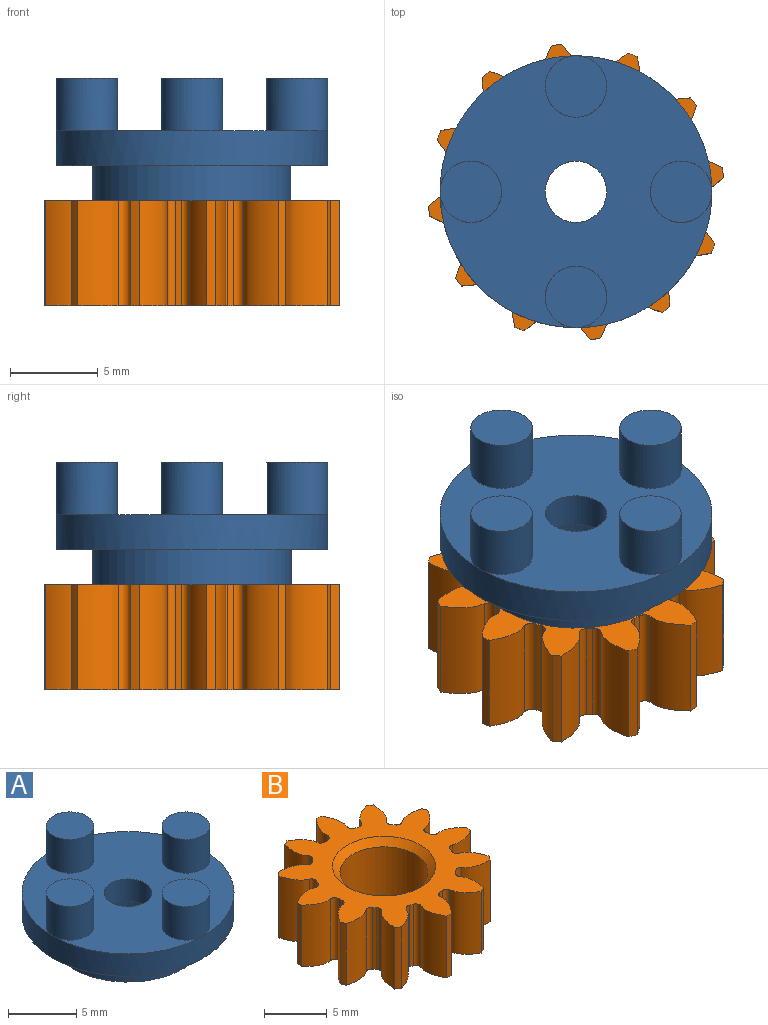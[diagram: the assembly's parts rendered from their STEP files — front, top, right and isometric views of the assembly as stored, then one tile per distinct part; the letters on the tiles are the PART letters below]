
ASSEMBLY  parts=2 mates=1
PART A: 16 faces, bbox 22.5x22.5x14 mm
  f0: plane 7x7mm, normal (0,0,-1), area 28.9mm2, adj f1,f13
  f1: cylinder r=1.75mm len=3.5mm, axis (0,0,-1), area 22mm2, adj f0,f3
  f2: cylinder r=7.75mm len=15.5mm, axis (0,0,-1), area 97.4mm2, adj f3,f4
  f3: plane 15.5x15.5mm, normal (0,0,1), area 140.6mm2, adj f1,f2,f5,f7,f9,f11
  f4: plane 15.5x15.5mm, normal (0,0,-1), area 88.4mm2, adj f2,f14
  f5: cylinder r=1.75mm len=3.5mm, axis (0,0,-1), area 33mm2, adj f3,f6
  f6: plane 3.5x3.5mm, normal (0,0,1), area 9.6mm2, adj f5
  f7: cylinder r=1.75mm len=3.5mm, axis (0,0,-1), area 33mm2, adj f3,f8
  f8: plane 10.5x10.5mm, normal (0,0,1), area 19.2mm2, adj f7
  f9: cylinder r=1.75mm len=3.5mm, axis (0,0,-1), area 33mm2, adj f3,f10
  f10: plane 3.5x3.5mm, normal (0,0,1), area 9.6mm2, adj f9
  f11: cylinder r=1.75mm len=3.5mm, axis (0,0,-1), area 33mm2, adj f3,f12
  f12: plane 3.5x3.5mm, normal (0,0,1), area 9.6mm2, adj f11
  f13: cylinder r=3.5mm len=7mm, axis (0,0,1), area 44mm2, adj f0,f15
  f14: cylinder r=5.65mm len=11.3mm, axis (0,0,1), area 71mm2, adj f4,f15
  f15: plane 11.3x11.3mm, normal (0,0,-1), area 61.8mm2, adj f13,f14
PART B: 76 faces, bbox 16.9x16.9x6 mm
  f0: cylinder r=8.46mm len=6mm, axis (0,0,-1), area 3.2mm2, adj f11,f14,f62,f71
  f1: cylinder r=8.46mm len=6mm, axis (0,0,-1), area 3.2mm2, adj f11,f14,f66,f72
  f2: cylinder r=8.46mm len=6mm, axis (0,0,-1), area 3.2mm2, adj f11,f14,f57,f61
  f3: cylinder r=8.46mm len=6mm, axis (0,0,-1), area 3.2mm2, adj f11,f14,f52,f56
  f4: cylinder r=8.46mm len=6mm, axis (0,0,-1), area 3.2mm2, adj f11,f14,f47,f51
  f5: cylinder r=8.46mm len=6mm, axis (0,0,-1), area 3.2mm2, adj f11,f14,f37,f46
  f6: cylinder r=8.46mm len=6mm, axis (0,0,-1), area 3.2mm2, adj f11,f14,f17,f41
  f7: cylinder r=8.46mm len=6mm, axis (0,0,-1), area 3.2mm2, adj f11,f14,f36,f42
  f8: cylinder r=8.46mm len=6mm, axis (0,0,-1), area 3.2mm2, adj f11,f14,f27,f31
  f9: cylinder r=8.46mm len=6mm, axis (0,0,-1), area 3.2mm2, adj f11,f14,f22,f26
  f10: cylinder r=8.46mm len=6mm, axis (0,0,-1), area 3.2mm2, adj f11,f14,f21,f67
  f11: plane 16.87x16.87mm, normal (0,0,1), area 106.9mm2, adj f0,f1,f2,f3,f4,f5,f6,f7
  f12: cylinder r=3.5mm len=7mm, axis (0,0,-1), area 118.8mm2, adj f14,f75
  f13: cylinder r=8.46mm len=6mm, axis (0,0,-1), area 3.2mm2, adj f11,f14,f16,f32
  f14: plane 16.87x16.87mm, normal (0,0,-1), area 121.2mm2, adj f0,f1,f2,f3,f4,f5,f6,f7
  f15: cylinder r=5.74mm len=6mm, axis (0,0,-1), area 2.2mm2, adj f11,f14,f18,f19
  f16: extruded ~6x2.27mm, area 15.5mm2, adj f11,f13,f14,f18
  f17: extruded ~6x1.92mm, area 15.5mm2, adj f6,f11,f14,f19
  f18: cylinder r=0.43mm len=6mm, axis (0,0,-1), area 3.9mm2, adj f11,f14,f15,f16
  f19: cylinder r=0.43mm len=6mm, axis (0,0,-1), area 3.9mm2, adj f11,f14,f15,f17
  f20: cylinder r=5.74mm len=6mm, axis (0,0,-1), area 2.2mm2, adj f11,f14,f23,f24
  f21: extruded ~6x2.27mm, area 15.5mm2, adj f10,f11,f14,f23
  f22: extruded ~6x1.92mm, area 15.5mm2, adj f9,f11,f14,f24
  f23: cylinder r=0.43mm len=6mm, axis (0,0,-1), area 3.9mm2, adj f11,f14,f20,f21
  f24: cylinder r=0.43mm len=6mm, axis (0,0,-1), area 3.9mm2, adj f11,f14,f20,f22
  f25: cylinder r=5.74mm len=6mm, axis (0,0,-1), area 2.2mm2, adj f11,f14,f28,f29
  f26: extruded ~6x2.47mm, area 15.5mm2, adj f9,f11,f14,f28
  f27: extruded ~6x2.33mm, area 15.5mm2, adj f8,f11,f14,f29
  f28: cylinder r=0.43mm len=6mm, axis (0,0,-1), area 3.9mm2, adj f11,f14,f25,f26
  f29: cylinder r=0.43mm len=6mm, axis (0,0,-1), area 3.9mm2, adj f11,f14,f25,f27
  f30: cylinder r=5.74mm len=6mm, axis (0,0,-1), area 2.2mm2, adj f11,f14,f33,f34
  f31: extruded ~6x2.02mm, area 15.5mm2, adj f8,f11,f14,f33
  f32: extruded ~6x2.45mm, area 15.5mm2, adj f11,f13,f14,f34
  f33: cylinder r=0.43mm len=6mm, axis (0,0,-1), area 3.9mm2, adj f11,f14,f30,f31
  f34: cylinder r=0.43mm len=6mm, axis (0,0,-1), area 3.9mm2, adj f11,f14,f30,f32
  f35: cylinder r=5.74mm len=6mm, axis (0,0,-1), area 2.2mm2, adj f11,f14,f38,f39
  f36: extruded ~6x2.02mm, area 15.5mm2, adj f7,f11,f14,f38
  f37: extruded ~6x2.45mm, area 15.5mm2, adj f5,f11,f14,f39
  f38: cylinder r=0.43mm len=6mm, axis (0,0,-1), area 3.9mm2, adj f11,f14,f35,f36
  f39: cylinder r=0.43mm len=6mm, axis (0,0,-1), area 3.9mm2, adj f11,f14,f35,f37
  f40: cylinder r=5.74mm len=6mm, axis (0,0,-1), area 2.2mm2, adj f11,f14,f43,f44
  f41: extruded ~6x2.47mm, area 15.5mm2, adj f6,f11,f14,f43
  f42: extruded ~6x2.33mm, area 15.5mm2, adj f7,f11,f14,f44
  f43: cylinder r=0.43mm len=6mm, axis (0,0,-1), area 3.9mm2, adj f11,f14,f40,f41
  f44: cylinder r=0.43mm len=6mm, axis (0,0,-1), area 3.9mm2, adj f11,f14,f40,f42
  f45: cylinder r=5.74mm len=6mm, axis (0,0,-1), area 2.2mm2, adj f11,f14,f48,f49
  f46: extruded ~6x2.27mm, area 15.5mm2, adj f5,f11,f14,f48
  f47: extruded ~6x1.92mm, area 15.5mm2, adj f4,f11,f14,f49
  f48: cylinder r=0.43mm len=6mm, axis (0,0,-1), area 3.9mm2, adj f11,f14,f45,f46
  f49: cylinder r=0.43mm len=6mm, axis (0,0,-1), area 3.9mm2, adj f11,f14,f45,f47
  f50: cylinder r=5.74mm len=6mm, axis (0,0,-1), area 2.2mm2, adj f11,f14,f53,f54
  f51: extruded ~6x2.47mm, area 15.5mm2, adj f4,f11,f14,f53
  f52: extruded ~6x2.33mm, area 15.5mm2, adj f3,f11,f14,f54
  f53: cylinder r=0.43mm len=6mm, axis (0,0,-1), area 3.9mm2, adj f11,f14,f50,f51
  f54: cylinder r=0.43mm len=6mm, axis (0,0,-1), area 3.9mm2, adj f11,f14,f50,f52
  f55: cylinder r=5.74mm len=6mm, axis (0,0,-1), area 2.2mm2, adj f11,f14,f58,f59
  f56: extruded ~6x2.02mm, area 15.5mm2, adj f3,f11,f14,f58
  f57: extruded ~6x2.45mm, area 15.5mm2, adj f2,f11,f14,f59
  f58: cylinder r=0.43mm len=6mm, axis (0,0,-1), area 3.9mm2, adj f11,f14,f55,f56
  f59: cylinder r=0.43mm len=6mm, axis (0,0,-1), area 3.9mm2, adj f11,f14,f55,f57
  f60: cylinder r=5.74mm len=6mm, axis (0,0,-1), area 2.2mm2, adj f11,f14,f63,f64
  f61: extruded ~6x2.27mm, area 15.5mm2, adj f2,f11,f14,f63
  f62: extruded ~6x1.92mm, area 15.5mm2, adj f0,f11,f14,f64
  f63: cylinder r=0.43mm len=6mm, axis (0,0,-1), area 3.9mm2, adj f11,f14,f60,f61
  f64: cylinder r=0.43mm len=6mm, axis (0,0,-1), area 3.9mm2, adj f11,f14,f60,f62
  f65: cylinder r=5.74mm len=6mm, axis (0,0,-1), area 2.2mm2, adj f11,f14,f68,f69
  f66: extruded ~6x2.02mm, area 15.5mm2, adj f1,f11,f14,f68
  f67: extruded ~6x2.45mm, area 15.5mm2, adj f10,f11,f14,f69
  f68: cylinder r=0.43mm len=6mm, axis (0,0,-1), area 3.9mm2, adj f11,f14,f65,f66
  f69: cylinder r=0.43mm len=6mm, axis (0,0,-1), area 3.9mm2, adj f11,f14,f65,f67
  f70: cylinder r=5.74mm len=6mm, axis (0,0,-1), area 2.2mm2, adj f11,f14,f73,f74
  f71: extruded ~6x2.47mm, area 15.5mm2, adj f0,f11,f14,f73
  f72: extruded ~6x2.33mm, area 15.5mm2, adj f1,f11,f14,f74
  f73: cylinder r=0.43mm len=6mm, axis (0,0,-1), area 3.9mm2, adj f11,f14,f70,f71
  f74: cylinder r=0.43mm len=6mm, axis (0,0,-1), area 3.9mm2, adj f11,f14,f70,f72
  f75: cone r=3.5mm half-angle=45deg, axis (0,0,1), area 20.3mm2, adj f11,f12
PLACE A t=(34.95,-13.16,-22.14)mm
PLACE B rot(axis=(1,0,0),180deg) t=(27.7,-13.16,0.86)mm
MATE cylindrical B.f0 <-> A.f13  axis (0,0,1) through (34.95,-13.16,0.86)mm
